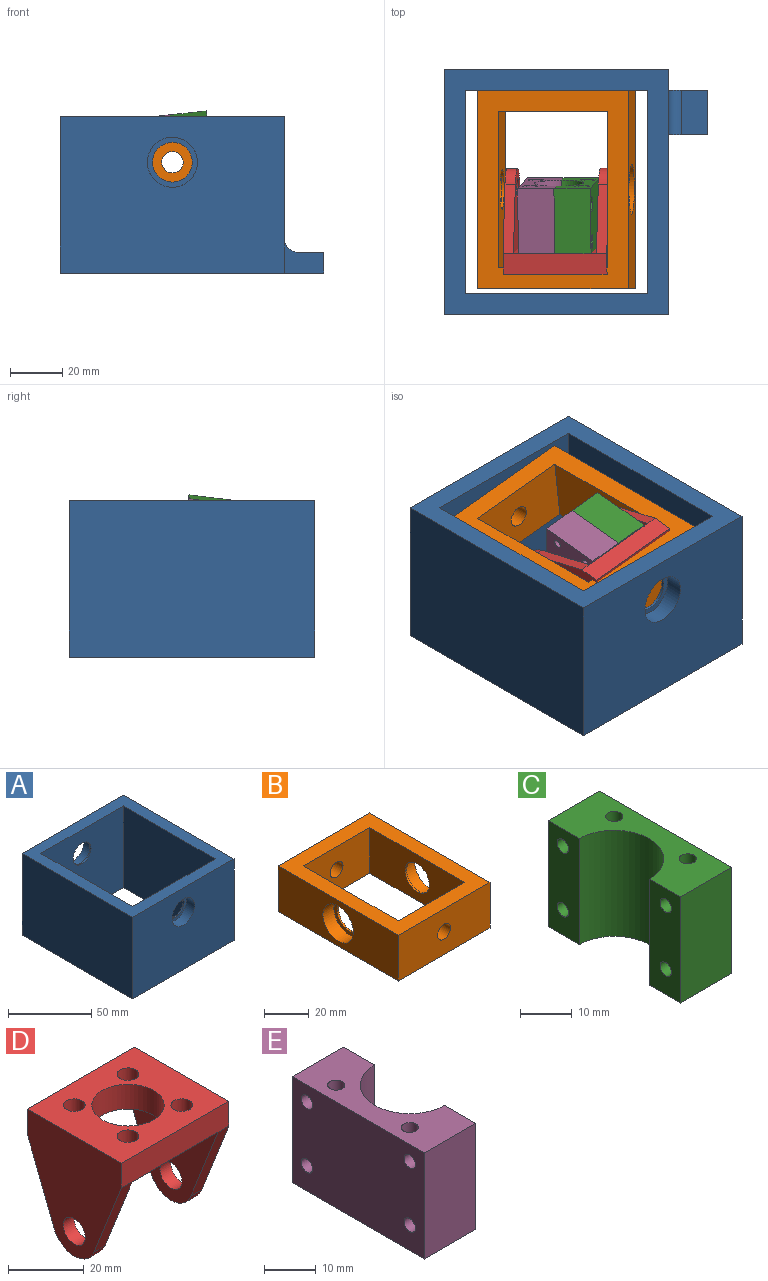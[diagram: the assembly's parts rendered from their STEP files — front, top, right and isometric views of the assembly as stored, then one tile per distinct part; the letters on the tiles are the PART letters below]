
ASSEMBLY  parts=5 mates=4
PART A: 21 faces, bbox 101x94x60 mm
  f0: cylinder r=9.6mm len=19.2mm, axis (0,-1,0), area 422.2mm2, adj f3,f14
  f1: plane 86x60mm, normal (0,1,0), area 4870.5mm2, adj f2,f8,f9,f10,f15
  f2: plane 94x60mm, normal (-1,0,0), area 5640mm2, adj f1,f3,f9,f15
  f3: plane 86x60mm, normal (0,-1,0), area 4870.5mm2, adj f0,f2,f8,f9,f15
  f4: plane 78x60mm, normal (-1,0,0), area 4680mm2, adj f5,f7,f9,f15
  f5: plane 70x60mm, normal (0,1,0), area 4018.5mm2, adj f4,f6,f9,f13,f15
  f6: plane 78x60mm, normal (1,0,0), area 4680mm2, adj f5,f7,f9,f15
  f7: plane 70x60mm, normal (0,-1,0), area 4018.5mm2, adj f4,f6,f9,f11,f15
  f8: plane 94x60mm, normal (1,0,0), area 5419mm2, adj f1,f3,f9,f15,f16,f18,f20
  f9: plane 94x86mm, normal (0,0,1), area 2624mm2, adj f1,f2,f3,f4,f5,f6,f7,f8
  f10: cylinder r=9.6mm len=19.2mm, axis (0,-1,0), area 422.2mm2, adj f1,f12
  f11: cylinder r=7.6mm len=15.2mm, axis (0,-1,0), area 47.8mm2, adj f7,f12
  f12: plane 19.2x19.2mm, normal (0,1,0), area 108.1mm2, adj f10,f11
  f13: cylinder r=7.6mm len=15.2mm, axis (0,1,0), area 47.8mm2, adj f5,f14
  f14: plane 19.2x19.2mm, normal (0,-1,0), area 108.1mm2, adj f0,f13
  f15: plane 101x94mm, normal (0,0,-1), area 2879mm2, adj f1,f2,f3,f4,f5,f6,f7,f8
  f16: plane 15x13mm, normal (0,1,0), area 125.4mm2, adj f8,f15,f17,f19,f20
  f17: plane 17x8mm, normal (1,0,0), area 136mm2, adj f15,f16,f18,f19
  f18: plane 15x13mm, normal (0,-1,0), area 125.4mm2, adj f8,f15,f17,f19,f20
  f19: plane 17x10mm, normal (0,0,1), area 170mm2, adj f16,f17,f18,f20
  f20: cylinder r=5mm len=17mm, axis (0,-1,0), area 133.5mm2, adj f8,f16,f18,f19
PART B: 18 faces, bbox 58x76x25 mm
  f0: cylinder r=9.62mm len=19.25mm, axis (-1,0,0), area 423.3mm2, adj f4,f15
  f1: plane 42x25mm, normal (0,-1,0), area 997.2mm2, adj f2,f8,f9,f10,f13
  f2: plane 60x25mm, normal (-1,0,0), area 1317.3mm2, adj f1,f3,f9,f10,f16
  f3: plane 42x25mm, normal (0,1,0), area 997.2mm2, adj f2,f8,f9,f10,f12
  f4: plane 76x25mm, normal (-1,0,0), area 1609mm2, adj f0,f5,f7,f9,f10
  f5: plane 58x25mm, normal (0,-1,0), area 1397.2mm2, adj f4,f6,f9,f10,f12
  f6: plane 76x25mm, normal (1,0,0), area 1609mm2, adj f5,f7,f9,f10,f11
  f7: plane 58x25mm, normal (0,1,0), area 1397.2mm2, adj f4,f6,f9,f10,f13
  f8: plane 60x25mm, normal (1,0,0), area 1317.3mm2, adj f1,f3,f9,f10,f14
  f9: plane 76x58mm, normal (0,0,1), area 1888mm2, adj f1,f2,f3,f4,f5,f6,f7,f8
  f10: plane 76x58mm, normal (0,0,-1), area 1888mm2, adj f1,f2,f3,f4,f5,f6,f7,f8
  f11: cylinder r=9.62mm len=19.25mm, axis (-1,0,0), area 423.3mm2, adj f6,f17
  f12: cylinder r=4.1mm len=8.2mm, axis (0,-1,0), area 206.1mm2, adj f3,f5
  f13: cylinder r=4.1mm len=8.2mm, axis (0,-1,0), area 206.1mm2, adj f1,f7
  f14: cylinder r=7.62mm len=15.25mm, axis (1,0,0), area 47.9mm2, adj f8,f15
  f15: plane 19.25x19.25mm, normal (-1,0,0), area 108.4mm2, adj f0,f14
  f16: cylinder r=7.62mm len=15.25mm, axis (-1,0,0), area 47.9mm2, adj f2,f17
  f17: plane 19.25x19.25mm, normal (1,0,0), area 108.4mm2, adj f11,f16
PART C: 56 faces, bbox 14x36x25 mm
  f0: cylinder r=1.66mm len=22.5mm, axis (0,0,1), area 235.4mm2, adj f11,f19,f42,f43,f44,f49,f50,f51
  f1: cylinder r=1.66mm len=22.5mm, axis (0,0,1), area 235.4mm2, adj f11,f12,f28,f29,f30,f35,f36,f37
  f2: plane 36x25mm, normal (1,0,0), area 787.5mm2, adj f7,f8,f10,f11,f28,f29,f31,f32
  f3: cylinder r=1.55mm len=11.5mm, axis (-1,0,0), area 112mm2, adj f27,f51
  f4: cylinder r=1.55mm len=11.5mm, axis (-1,0,0), area 112mm2, adj f27,f44
  f5: cylinder r=1.55mm len=11.5mm, axis (-1,0,0), area 112mm2, adj f26,f37
  f6: cylinder r=1.55mm len=11.5mm, axis (-1,0,0), area 112mm2, adj f26,f30
  f7: plane 36x14mm, normal (0,0,-1), area 305.2mm2, adj f2,f8,f9,f10,f13,f14,f15,f16
  f8: plane 25x14mm, normal (0,1,0), area 350mm2, adj f2,f7,f11,f26
  f9: cylinder r=9.53mm len=25mm, axis (0,0,-1), area 748.1mm2, adj f7,f11,f26,f27
  f10: plane 25x14mm, normal (0,-1,0), area 350mm2, adj f2,f7,f11,f27
  f11: plane 36x14mm, normal (0,0,1), area 344.1mm2, adj f0,f1,f2,f8,f9,f10,f26,f27
  f12: plane 6.58x5.7mm, normal (0,0,-1), area 19.4mm2, adj f1,f13,f14,f15,f16,f17,f18
  f13: plane 2.85x2.5mm, normal (0.87,-0.5,0), area 8.2mm2, adj f7,f12,f14,f18
  f14: plane 3.29x2.5mm, normal (0,-1,0), area 8.2mm2, adj f7,f12,f13,f15
  f15: plane 2.85x2.5mm, normal (-0.87,-0.5,0), area 8.2mm2, adj f7,f12,f14,f16
  f16: plane 2.85x2.5mm, normal (-0.87,0.5,0), area 8.2mm2, adj f7,f12,f15,f17
  f17: plane 3.29x2.5mm, normal (0,1,0), area 8.2mm2, adj f7,f12,f16,f18
  f18: plane 2.85x2.5mm, normal (0.87,0.5,0), area 8.2mm2, adj f7,f12,f13,f17
  f19: plane 6.58x5.7mm, normal (0,0,-1), area 19.4mm2, adj f0,f20,f21,f22,f23,f24,f25
  f20: plane 2.85x2.5mm, normal (0.87,0.5,0), area 8.2mm2, adj f7,f19,f21,f25
  f21: plane 2.85x2.5mm, normal (0.87,-0.5,0), area 8.2mm2, adj f7,f19,f20,f22
  f22: plane 3.29x2.5mm, normal (0,-1,0), area 8.2mm2, adj f7,f19,f21,f23
  f23: plane 2.85x2.5mm, normal (-0.87,-0.5,0), area 8.2mm2, adj f7,f19,f22,f24
  f24: plane 2.85x2.5mm, normal (-0.87,0.5,0), area 8.2mm2, adj f7,f19,f23,f25
  f25: plane 3.29x2.5mm, normal (0,1,0), area 8.2mm2, adj f7,f19,f20,f24
  f26: plane 25x8.48mm, normal (-1,0,0), area 196.8mm2, adj f5,f6,f7,f8,f9,f11
  f27: plane 25x8.48mm, normal (-1,0,0), area 196.8mm2, adj f3,f4,f7,f9,f10,f11
  f28: plane 2.85x2.5mm, normal (0,0.87,-0.5), area 8.2mm2, adj f1,f2,f29,f30,f34
  f29: plane 2.85x2.5mm, normal (0,0.87,0.5), area 8.2mm2, adj f1,f2,f28,f30,f31
  f30: plane 6.57x5.7mm, normal (1,0,0), area 20.6mm2, adj f1,f6,f28,f29,f31,f32,f33,f34
  f31: plane 3.29x2.5mm, normal (0,0,1), area 8.2mm2, adj f2,f29,f30,f32
  f32: plane 2.85x2.5mm, normal (0,-0.87,0.5), area 8.2mm2, adj f2,f30,f31,f33
  f33: plane 2.85x2.5mm, normal (0,-0.87,-0.5), area 8.2mm2, adj f2,f30,f32,f34
  f34: plane 3.29x2.5mm, normal (0,0,-1), area 8.2mm2, adj f2,f28,f30,f33
  f35: plane 2.85x2.5mm, normal (0,0.87,-0.5), area 8.2mm2, adj f1,f2,f36,f37,f40
  f36: plane 2.85x2.5mm, normal (0,0.87,0.5), area 8.2mm2, adj f1,f2,f35,f37,f41
  f37: plane 6.57x5.7mm, normal (1,0,0), area 20.6mm2, adj f1,f5,f35,f36,f38,f39,f40,f41
  f38: plane 2.85x2.5mm, normal (0,-0.87,0.5), area 8.2mm2, adj f2,f37,f39,f41
  f39: plane 2.85x2.5mm, normal (0,-0.87,-0.5), area 8.2mm2, adj f2,f37,f38,f40
  f40: plane 3.29x2.5mm, normal (0,0,-1), area 8.2mm2, adj f2,f35,f37,f39
  f41: plane 3.29x2.5mm, normal (0,0,1), area 8.2mm2, adj f2,f36,f37,f38
  f42: plane 2.85x2.5mm, normal (0,-0.87,0.5), area 8.2mm2, adj f0,f2,f43,f44,f47
  f43: plane 2.85x2.5mm, normal (0,-0.87,-0.5), area 8.2mm2, adj f0,f2,f42,f44,f48
  f44: plane 6.57x5.7mm, normal (1,0,0), area 20.6mm2, adj f0,f4,f42,f43,f45,f46,f47,f48
  f45: plane 2.85x2.5mm, normal (0,0.87,-0.5), area 8.2mm2, adj f2,f44,f46,f48
  f46: plane 2.85x2.5mm, normal (0,0.87,0.5), area 8.2mm2, adj f2,f44,f45,f47
  f47: plane 3.29x2.5mm, normal (0,0,1), area 8.2mm2, adj f2,f42,f44,f46
  f48: plane 3.29x2.5mm, normal (0,0,-1), area 8.2mm2, adj f2,f43,f44,f45
  f49: plane 2.85x2.5mm, normal (0,-0.87,0.5), area 8.2mm2, adj f0,f2,f50,f51,f54
  f50: plane 2.85x2.5mm, normal (0,-0.87,-0.5), area 8.2mm2, adj f0,f2,f49,f51,f55
  f51: plane 6.57x5.7mm, normal (1,0,0), area 20.6mm2, adj f0,f3,f49,f50,f52,f53,f54,f55
  f52: plane 2.85x2.5mm, normal (0,0.87,-0.5), area 8.2mm2, adj f2,f51,f53,f55
  f53: plane 2.85x2.5mm, normal (0,0.87,0.5), area 8.2mm2, adj f2,f51,f52,f54
  f54: plane 3.29x2.5mm, normal (0,0,1), area 8.2mm2, adj f2,f49,f51,f53
  f55: plane 3.29x2.5mm, normal (0,0,-1), area 8.2mm2, adj f2,f50,f51,f52
PART D: 29 faces, bbox 40x35x38.7 mm
  f0: plane 35x32mm, normal (0,0,-1), area 804.8mm2, adj f1,f3,f4,f11,f16,f17,f18,f19
  f1: plane 40x8mm, normal (0,-1,0), area 320mm2, adj f0,f2,f5,f6,f7,f15
  f2: plane 38.65x35mm, normal (1,0,0), area 920.1mm2, adj f1,f3,f6,f12,f13,f14,f15
  f3: plane 40x8mm, normal (0,1,0), area 320mm2, adj f0,f2,f5,f6,f8,f13
  f4: cylinder r=9.53mm len=19.05mm, axis (0,0,-1), area 478.8mm2, adj f0,f6
  f5: plane 38.65x35mm, normal (-1,0,0), area 920.1mm2, adj f1,f3,f6,f7,f8,f9,f10
  f6: plane 40x35mm, normal (0,0,1), area 1012.9mm2, adj f1,f2,f3,f4,f5,f21,f23,f25
  f7: plane 25.58x10.05mm, normal (0,-0.93,-0.37), area 109.9mm2, adj f1,f5,f10,f11
  f8: plane 25.58x10.05mm, normal (0,0.93,-0.37), area 109.9mm2, adj f3,f5,f10,f11
  f9: cylinder r=4.1mm len=8.2mm, axis (-1,0,0), area 103mm2, adj f5,f11
  f10: cylinder r=8mm len=14.89mm, axis (-1,0,0), area 76.6mm2, adj f5,f7,f8,f11
  f11: plane 35x30.65mm, normal (1,0,0), area 640.1mm2, adj f0,f7,f8,f9,f10
  f12: cylinder r=8mm len=14.89mm, axis (1,0,0), area 76.6mm2, adj f2,f13,f15,f16
  f13: plane 25.58x10.05mm, normal (0,0.93,-0.37), area 109.9mm2, adj f2,f3,f12,f16
  f14: cylinder r=4.1mm len=8.2mm, axis (1,0,0), area 103mm2, adj f2,f16
  f15: plane 25.58x10.05mm, normal (0,-0.93,-0.37), area 109.9mm2, adj f1,f2,f12,f16
  f16: plane 35x30.65mm, normal (-1,0,0), area 640.1mm2, adj f0,f12,f13,f14,f15
  f17: cylinder r=1.55mm len=3.1mm, axis (0,0,1), area 29.2mm2, adj f0,f28
  f18: cylinder r=1.55mm len=3.1mm, axis (0,0,1), area 29.2mm2, adj f0,f26
  f19: cylinder r=1.55mm len=3.1mm, axis (0,0,1), area 29.2mm2, adj f0,f24
  f20: cylinder r=1.55mm len=3.1mm, axis (0,0,1), area 29.2mm2, adj f0,f22
  f21: cylinder r=2.85mm len=5.7mm, axis (0,0,1), area 89.5mm2, adj f6,f22
  f22: plane 5.7x5.7mm, normal (0,0,1), area 18mm2, adj f20,f21
  f23: cylinder r=2.85mm len=5.7mm, axis (0,0,1), area 89.5mm2, adj f6,f24
  f24: plane 5.7x5.7mm, normal (0,0,1), area 18mm2, adj f19,f23
  f25: cylinder r=2.85mm len=5.7mm, axis (0,0,1), area 89.5mm2, adj f6,f26
  f26: plane 5.7x5.7mm, normal (0,0,1), area 18mm2, adj f18,f25
  f27: cylinder r=2.85mm len=5.7mm, axis (0,0,1), area 89.5mm2, adj f6,f28
  f28: plane 5.7x5.7mm, normal (0,0,1), area 18mm2, adj f17,f27
PART E: 28 faces, bbox 14x36x25 mm
  f0: plane 25x8.48mm, normal (1,0,0), area 196.8mm2, adj f18,f19,f20,f22,f26,f27
  f1: plane 6.58x5.7mm, normal (0,0,-1), area 19.4mm2, adj f9,f10,f11,f12,f13,f14,f16
  f2: plane 6.58x5.7mm, normal (0,0,-1), area 19.4mm2, adj f3,f4,f5,f6,f7,f8,f17
  f3: plane 2.85x2.5mm, normal (0.87,-0.5,0), area 8.2mm2, adj f2,f4,f8,f22
  f4: plane 3.29x2.5mm, normal (0,-1,0), area 8.2mm2, adj f2,f3,f5,f22
  f5: plane 2.85x2.5mm, normal (-0.87,-0.5,0), area 8.2mm2, adj f2,f4,f6,f22
  f6: plane 2.85x2.5mm, normal (-0.87,0.5,0), area 8.2mm2, adj f2,f5,f7,f22
  f7: plane 3.29x2.5mm, normal (0,1,0), area 8.2mm2, adj f2,f6,f8,f22
  f8: plane 2.85x2.5mm, normal (0.87,0.5,0), area 8.2mm2, adj f2,f3,f7,f22
  f9: plane 2.85x2.5mm, normal (0.87,-0.5,0), area 8.2mm2, adj f1,f10,f14,f22
  f10: plane 3.29x2.5mm, normal (0,-1,0), area 8.2mm2, adj f1,f9,f11,f22
  f11: plane 2.85x2.5mm, normal (-0.87,-0.5,0), area 8.2mm2, adj f1,f10,f12,f22
  f12: plane 2.85x2.5mm, normal (-0.87,0.5,0), area 8.2mm2, adj f1,f11,f13,f22
  f13: plane 3.29x2.5mm, normal (0,1,0), area 8.2mm2, adj f1,f12,f14,f22
  f14: plane 2.85x2.5mm, normal (0.87,0.5,0), area 8.2mm2, adj f1,f9,f13,f22
  f15: plane 36x25mm, normal (-1,0,0), area 869.8mm2, adj f18,f19,f21,f22,f24,f25,f26,f27
  f16: cylinder r=1.66mm len=22.5mm, axis (0,0,1), area 235.4mm2, adj f1,f18
  f17: cylinder r=1.66mm len=22.5mm, axis (0,0,1), area 235.4mm2, adj f2,f18
  f18: plane 36x14mm, normal (0,0,1), area 344.1mm2, adj f0,f15,f16,f17,f19,f20,f21,f23
  f19: plane 25x14mm, normal (0,-1,0), area 350mm2, adj f0,f15,f18,f22
  f20: cylinder r=9.53mm len=25mm, axis (0,0,-1), area 748.1mm2, adj f0,f18,f22,f23
  f21: plane 25x14mm, normal (0,1,0), area 350mm2, adj f15,f18,f22,f23
  f22: plane 36x14mm, normal (0,0,-1), area 305.2mm2, adj f0,f3,f4,f5,f6,f7,f8,f9
  f23: plane 25x8.48mm, normal (1,0,0), area 196.8mm2, adj f18,f20,f21,f22,f24,f25
  f24: cylinder r=1.55mm len=14mm, axis (-1,0,0), area 136.3mm2, adj f15,f23
  f25: cylinder r=1.55mm len=14mm, axis (-1,0,0), area 136.3mm2, adj f15,f23
  f26: cylinder r=1.55mm len=14mm, axis (-1,0,0), area 136.3mm2, adj f0,f15
  f27: cylinder r=1.55mm len=14mm, axis (-1,0,0), area 136.3mm2, adj f0,f15
PLACE A t=(1.59,0.93,11.34)mm fixed
PLACE B rot(axis=(0,-1,0),6.2deg) t=(2.95,1.93,16.41)mm
PLACE C rot(axis=(1,-0.05,0.05),97.2deg) t=(2.55,4.26,29.23)mm
PLACE D rot(axis=(1,-0.05,0.05),97.2deg) t=(2.88,-20.56,26.2)mm
PLACE E rot(axis=(1,-0.05,0.05),97.2deg) t=(2.55,4.26,29.23)mm
MATE revolute B.f12 <-> A.f0  axis (0,1,0) through (1.59,39.93,28.84)mm
MATE fastened C.f9 <-> D.f4  axis (0.01,-0.99,-0.12) through (2.88,-20.56,26.2)mm
MATE fastened E.f20 <-> D.f4  axis (0.01,-0.99,-0.12) through (2.88,-20.56,26.2)mm
MATE revolute D.f9 <-> B.f0  axis (0.99,0,0.11) through (22.47,1.93,31.12)mm
